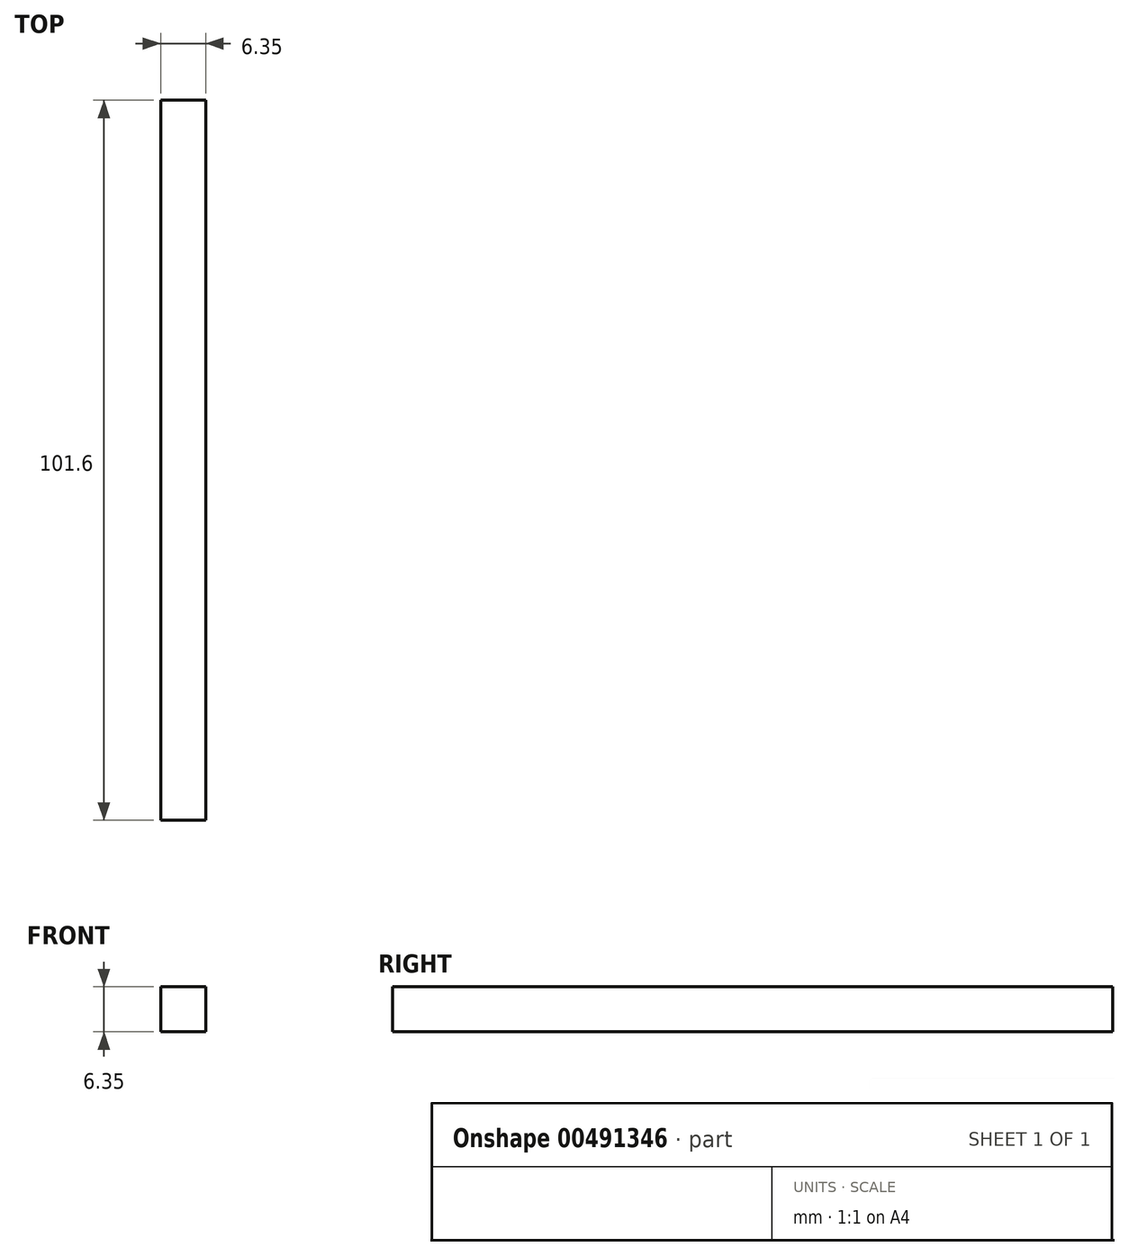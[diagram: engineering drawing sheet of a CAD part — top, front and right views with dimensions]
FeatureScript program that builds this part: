
annotation { "Feature Type Name" : "Feature", "Feature Type Description" : "" }
export const myFeature = defineFeature(function(context is Context, id is Id, definition is map)
    precondition{}
    {
        {
            var Q0;
            Q0=qCreatedBy(makeId("Front.planeOp"),FACE);
            var sketch = newSketch(context, id + "F0", { "sketchPlane" : qUnion([Q0])});
            skLineSegment(sketch, "E0.bottom", {"start": v(0, 0) * mm, "end": v(6.35, 0) * mm});
            skLineSegment(sketch, "E0.top", {"start": v(0, 6.35) * mm, "end": v(6.35, 6.35) * mm});
            skLineSegment(sketch, "E0.left", {"start": v(0, 0) * mm, "end": v(0, 6.35) * mm});
            skLineSegment(sketch, "E0.right", {"start": v(6.35, 0) * mm, "end": v(6.35, 6.35) * mm});
            skSolve(sketch);
        }
        {
            var Q0;
            Q0=makeQuery(id+"F0.imprint","IMPRINT",FACE,{"disambiguationData":[TD([[makeQuery(id+"F0.imprint","IMPRINT",EDGE,{"derivedFrom":sQuery(id+"F0.wireOp",EDGE,"E0.bottom")}),1.0]])]});
            extrude(context, id + "F1", {"entities" : qUnion([Q0]), "depth" : 101.6 * mm});
        }
    });
